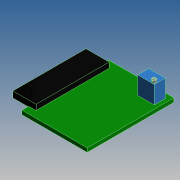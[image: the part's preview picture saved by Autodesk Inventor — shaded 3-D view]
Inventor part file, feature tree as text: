
AUTODESK INVENTOR PART (.ipt)
format: ipt  version: 2015 SP1 (Build 190203100, 203)  size: 232,448 bytes
history: native  units: mm
features: extrude x5, sketch x5
ambient origin geometry x8: Origin, YZ Plane, XZ Plane, XY Plane, X Axis, Y Axis, Z Axis, Center Point
bodies: Solid1 (feature_tree)
feature tree (10):
  extrude  "Extrusion1"  Depth=35.6mm
  extrude  "Extrusion2"  Depth=2.0mm
  extrude  "Extrusion3"  Depth=6.8mm
  extrude  "Extrusion4"  Depth=7.3mm TaperAngle=0.0deg
  extrude  "Extrusion5"  Depth=1.0mm
  sketch  "Sketch1"  dims[d0=26.8mm d1=35.6mm]
  sketch  "Sketch3"  dims[d2=1.6mm d3=0.0mm d4=2.0mm]
  sketch  "Sketch4"  dims[d5=1.5mm d6=6.8mm]
  sketch  "Sketch5"  dims[d7=4.6mm d8=7.3mm d9=0.0mm]
  sketch  "Sketch6"  dims[d10=1.7mm d11=1.0mm d12=1.0mm d13=1.0mm d14=0.0mm d15=0.5mm d16=0.5mm d17=0.0mm d18=0.3mm d19=2.5mm d20=6.5mm d21=3.0mm d22=30.0mm d23=0.0mm]
